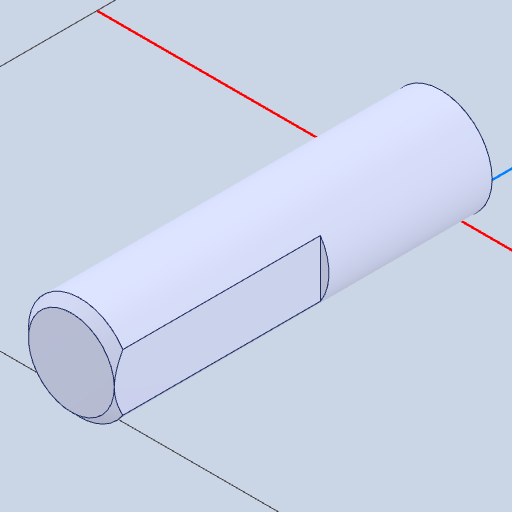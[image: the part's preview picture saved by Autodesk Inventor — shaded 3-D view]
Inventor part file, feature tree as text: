
AUTODESK INVENTOR PART (.ipt)
format: ipt  version: 2022 (Build 260153000, 153)  size: 101,888 bytes
history: native  units: mm
features: other x1, chamfer x1
ambient origin geometry x8: Origin, YZ Plane, XZ Plane, XY Plane, X Axis, Y Axis, Z Axis, Center Point
bodies: Body1 (feature_tree)
feature tree (2):
  other  "Твердое тело1"
  chamfer  "Chamfer1"  [1 undecoded]
note: 1 required parameter value undecoded (feature->parameter linkage not recoverable at this tier; creation-order binding heuristic only, values carry confidence <= 0.55)
